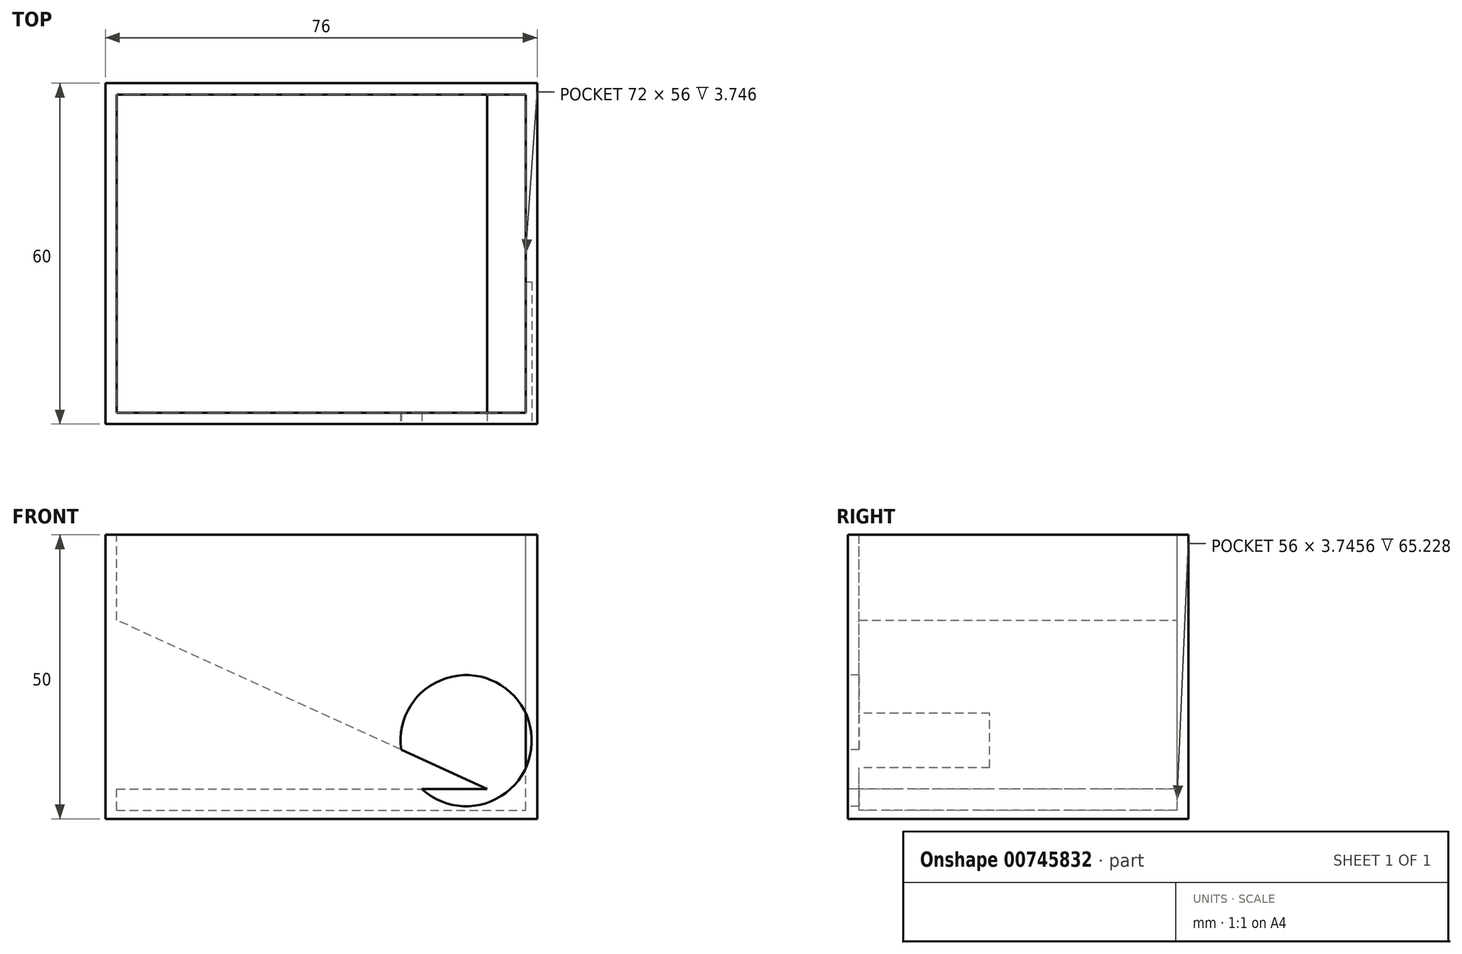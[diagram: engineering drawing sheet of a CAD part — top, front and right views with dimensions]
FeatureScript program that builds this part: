
annotation { "Feature Type Name" : "Feature", "Feature Type Description" : "" }
export const myFeature = defineFeature(function(context is Context, id is Id, definition is map)
    precondition{}
    {
        {
            var Q0;
            Q0=qCreatedBy(makeId("Front.planeOp"),FACE);
            var sketch = newSketch(context, id + "F0", { "sketchPlane" : qUnion([Q0])});
            skLineSegment(sketch, "E0.bottom", {"start": v(-36.82, 14.75) * mm, "end": v(39.18, 14.75) * mm});
            skLineSegment(sketch, "E0.top", {"start": v(-36.82, -35.25) * mm, "end": v(39.18, -35.25) * mm});
            skLineSegment(sketch, "E0.left", {"start": v(-36.82, 14.75) * mm, "end": v(-36.82, -35.25) * mm});
            skLineSegment(sketch, "E0.right", {"start": v(39.18, 14.75) * mm, "end": v(39.18, -35.25) * mm});
            skSolve(sketch);
        }
        {
            var Q0;
            Q0 = qSketchRegion(id + "F0", true);
            extrude(context, id + "F1", {"entities" : qUnion([Q0]), "oppositeDirection" : true, "depth" : 60 * mm, "offsetDistance" : 25 * mm});
        }
        {
            var Q0;
            Q0=makeQuery(id+"F1.opExtrude","SWEPT_FACE",FACE,{"disambiguationData":[OSD([sQuery(id+"F0.wireOp",EDGE,"E0.bottom")])]});
            var sketch = newSketch(context, id + "F2", { "sketchPlane" : qUnion([Q0])});
            skLineSegment(sketch, "E1.bottom", {"start": v(-34.82, 58) * mm, "end": v(37.18, 58) * mm});
            skLineSegment(sketch, "E1.top", {"start": v(-34.82, 2) * mm, "end": v(37.18, 2) * mm});
            skLineSegment(sketch, "E1.left", {"start": v(-34.82, 58) * mm, "end": v(-34.82, 2) * mm});
            skLineSegment(sketch, "E1.right", {"start": v(37.18, 58) * mm, "end": v(37.18, 2) * mm});
            skSolve(sketch);
        }
        {
            var Q0;
            Q0 = qSketchRegion(id + "F2", true);
            extrude(context, id + "F3", {"entities" : qUnion([Q0]), "operationType" : NewBodyOperationType.REMOVE, "oppositeDirection" : true, "depth" : 48.5 * mm, "offsetDistance" : 25 * mm});
        }
        {
            var Q0;
            Q0=makeQuery(id+"F1.opExtrude","CAP_FACE",FACE,{"disambiguationData":[OSD([sQuery(id+"F0.wireOp",EDGE,"E0.bottom"),sQuery(id+"F0.wireOp",EDGE,"E0.top"),sQuery(id+"F0.wireOp",EDGE,"E0.left"),sQuery(id+"F0.wireOp",EDGE,"E0.right")])],"isStart":true});
            var sketch = newSketch(context, id + "F4", { "sketchPlane" : qUnion([Q0])});
            skCircle(sketch, "E2", {"center": v(26.68, -21.5) * mm, "radius": 11.54 * mm});
            skSolve(sketch);
        }
        {
            var Q0;
            Q0 = qSketchRegion(id + "F4", true);
            extrude(context, id + "F5", {"entities" : qUnion([Q0]), "operationType" : NewBodyOperationType.REMOVE, "oppositeDirection" : true, "depth" : 25 * mm, "offsetDistance" : 25 * mm});
        }
        {
            var Q0;
            Q0=qCreatedBy(makeId("Front.planeOp"),FACE);
            var sketch = newSketch(context, id + "F6", { "sketchPlane" : qUnion([Q0])});
            skLineSegment(sketch, "E3", {"start": v(-35.4, -30) * mm, "end": v(30.41, -30) * mm});
            skLineSegment(sketch, "E4", {"start": v(30.41, -30) * mm, "end": v(-35.4, 0) * mm});
            skLineSegment(sketch, "E5", {"start": v(-35.4, 0) * mm, "end": v(-35.4, -30) * mm});
            skSolve(sketch);
        }
        {
            var Q0;
            Q0 = qSketchRegion(id + "F6", true);
            extrude(context, id + "F7", {"entities" : qUnion([Q0]), "operationType" : NewBodyOperationType.ADD, "oppositeDirection" : true, "depth" : 58 * mm, "offsetDistance" : 25 * mm});
        }
    });
